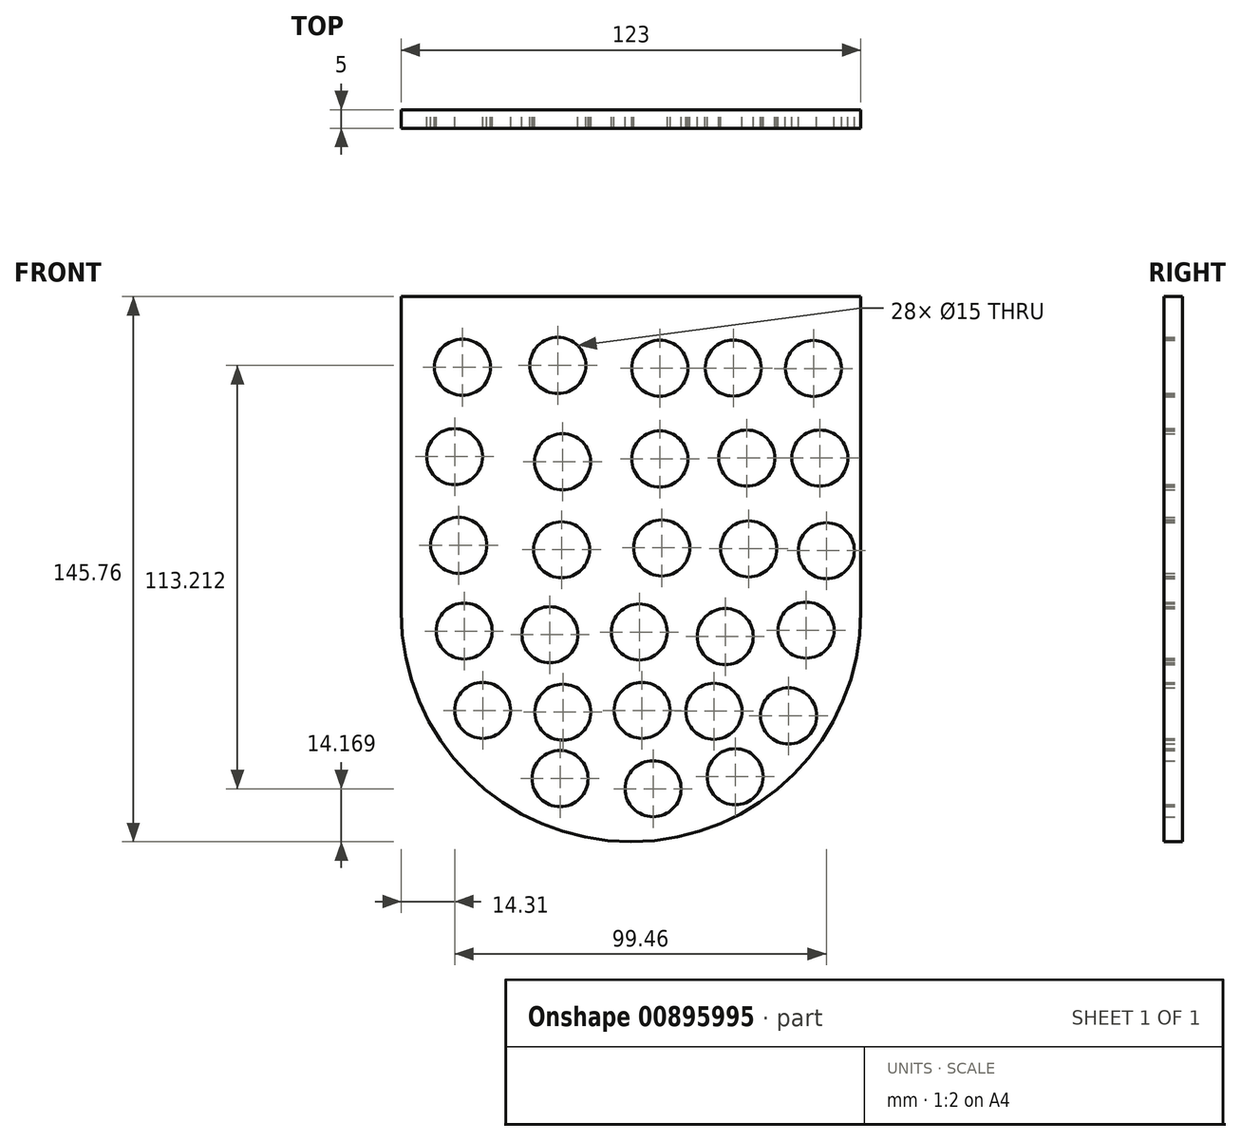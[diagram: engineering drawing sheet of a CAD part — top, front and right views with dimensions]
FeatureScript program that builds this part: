
annotation { "Feature Type Name" : "Feature", "Feature Type Description" : "" }
export const myFeature = defineFeature(function(context is Context, id is Id, definition is map)
    precondition{}
    {
        {
            var Q0;
            Q0=qCreatedBy(makeId("Front.planeOp"),FACE);
            var sketch = newSketch(context, id + "F0", { "sketchPlane" : qUnion([Q0])});
            skLineSegment(sketch, "E0.bottom", {"start": v(-86.71, 10.08) * mm, "end": v(36.29, 10.08) * mm});
            skLineSegment(sketch, "E0.top", {"start": v(-86.71, 94.34) * mm, "end": v(36.29, 94.34) * mm});
            skLineSegment(sketch, "E0.left", {"start": v(-86.71, 10.08) * mm, "end": v(-86.71, 94.34) * mm});
            skLineSegment(sketch, "E0.right", {"start": v(36.29, 10.08) * mm, "end": v(36.29, 94.34) * mm});
            skArc(sketch, "E1", {"start": v(-86.71, 10.08) * mm, "mid": v(-25.21, -51.42) * mm, "end": v(36.29, 10.08) * mm});
            skCircle(sketch, "E2", {"center": v(-70.3, 75.46) * mm, "radius": 7.5 * mm});
            skCircle(sketch, "E3", {"center": v(-44.78, 75.96) * mm, "radius": 7.5 * mm});
            skCircle(sketch, "E4", {"center": v(-17.5, 75.2) * mm, "radius": 7.5 * mm});
            skCircle(sketch, "E5", {"center": v(23.6, 75.15) * mm, "radius": 7.5 * mm});
            skCircle(sketch, "E6", {"center": v(25.3, 51.18) * mm, "radius": 7.5 * mm});
            skCircle(sketch, "E7", {"center": v(5.78, 51.18) * mm, "radius": 7.5 * mm});
            skCircle(sketch, "E8", {"center": v(-17.5, 50.93) * mm, "radius": 7.5 * mm});
            skCircle(sketch, "E9", {"center": v(-43.53, 50.18) * mm, "radius": 7.5 * mm});
            skCircle(sketch, "E10", {"center": v(-72.4, 51.56) * mm, "radius": 7.5 * mm});
            skCircle(sketch, "E11", {"center": v(-71.32, 27.84) * mm, "radius": 7.5 * mm});
            skCircle(sketch, "E12", {"center": v(-43.78, 26.65) * mm, "radius": 7.5 * mm});
            skCircle(sketch, "E13", {"center": v(27.06, 26.4) * mm, "radius": 7.5 * mm});
            skCircle(sketch, "E14", {"center": v(-69.84, 4.91) * mm, "radius": 7.5 * mm});
            skCircle(sketch, "E15", {"center": v(-46.9, 3.93) * mm, "radius": 7.5 * mm});
            skCircle(sketch, "E16", {"center": v(-23, 4.67) * mm, "radius": 7.5 * mm});
            skCircle(sketch, "E17", {"center": v(0, 3.43) * mm, "radius": 7.5 * mm});
            skCircle(sketch, "E18", {"center": v(21.64, 5.16) * mm, "radius": 7.5 * mm});
            skCircle(sketch, "E19", {"center": v(16.95, -17.77) * mm, "radius": 7.5 * mm});
            skCircle(sketch, "E20", {"center": v(-3.02, -16.54) * mm, "radius": 7.5 * mm});
            skCircle(sketch, "E21", {"center": v(-22.25, -16.3) * mm, "radius": 7.5 * mm});
            skCircle(sketch, "E22", {"center": v(-64.9, -16.3) * mm, "radius": 7.5 * mm});
            skCircle(sketch, "E23", {"center": v(-43.46, -16.79) * mm, "radius": 7.5 * mm});
            skCircle(sketch, "E24", {"center": v(-44.2, -34.54) * mm, "radius": 7.5 * mm});
            skCircle(sketch, "E25", {"center": v(2.65, -34.05) * mm, "radius": 7.5 * mm});
            skCircle(sketch, "E26", {"center": v(2.14, 75.25) * mm, "radius": 7.5 * mm});
            skCircle(sketch, "E27", {"center": v(-19.3, -37.25) * mm, "radius": 7.5 * mm});
            skCircle(sketch, "E28", {"center": v(6.28, 26.9) * mm, "radius": 7.5 * mm});
            skCircle(sketch, "E29", {"center": v(-17, 27.15) * mm, "radius": 7.5 * mm});
            skSolve(sketch);
        }
        {
            var Q0;
            Q0 = qSketchRegion(id + "F0", true);
            extrude(context, id + "F1", {"entities" : qUnion([Q0]), "depth" : 5 * mm, "offsetDistance" : 25 * mm});
        }
    });
